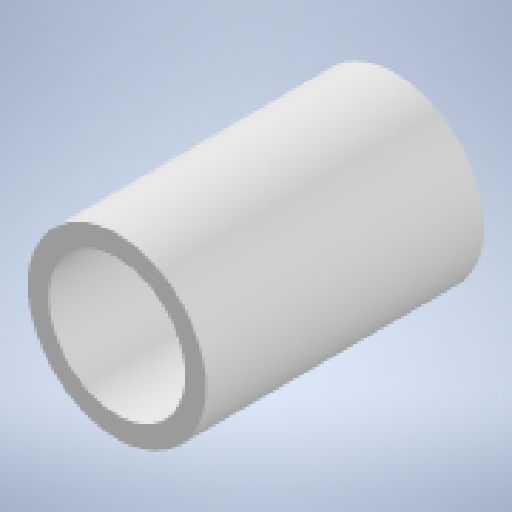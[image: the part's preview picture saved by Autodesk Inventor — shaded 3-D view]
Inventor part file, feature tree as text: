
AUTODESK INVENTOR PART (.ipt)
format: ipt  version: 2023.1 (Build 271208000, 208)  size: 137,728 bytes
history: native  units: mm
features: extrude x1, sketch x1
ambient origin geometry x8: Origin, YZ Plane, XZ Plane, XY Plane, X Axis, Y Axis, Z Axis, Center Point
bodies: Solid1 (feature_tree)
feature tree (2):
  extrude  "Extrusion1"  Depth=20.0mm
  sketch  "Sketch1"  dims[d0=12.8mm d1=1.5mm d2=20.0mm d3=0.0mm]
